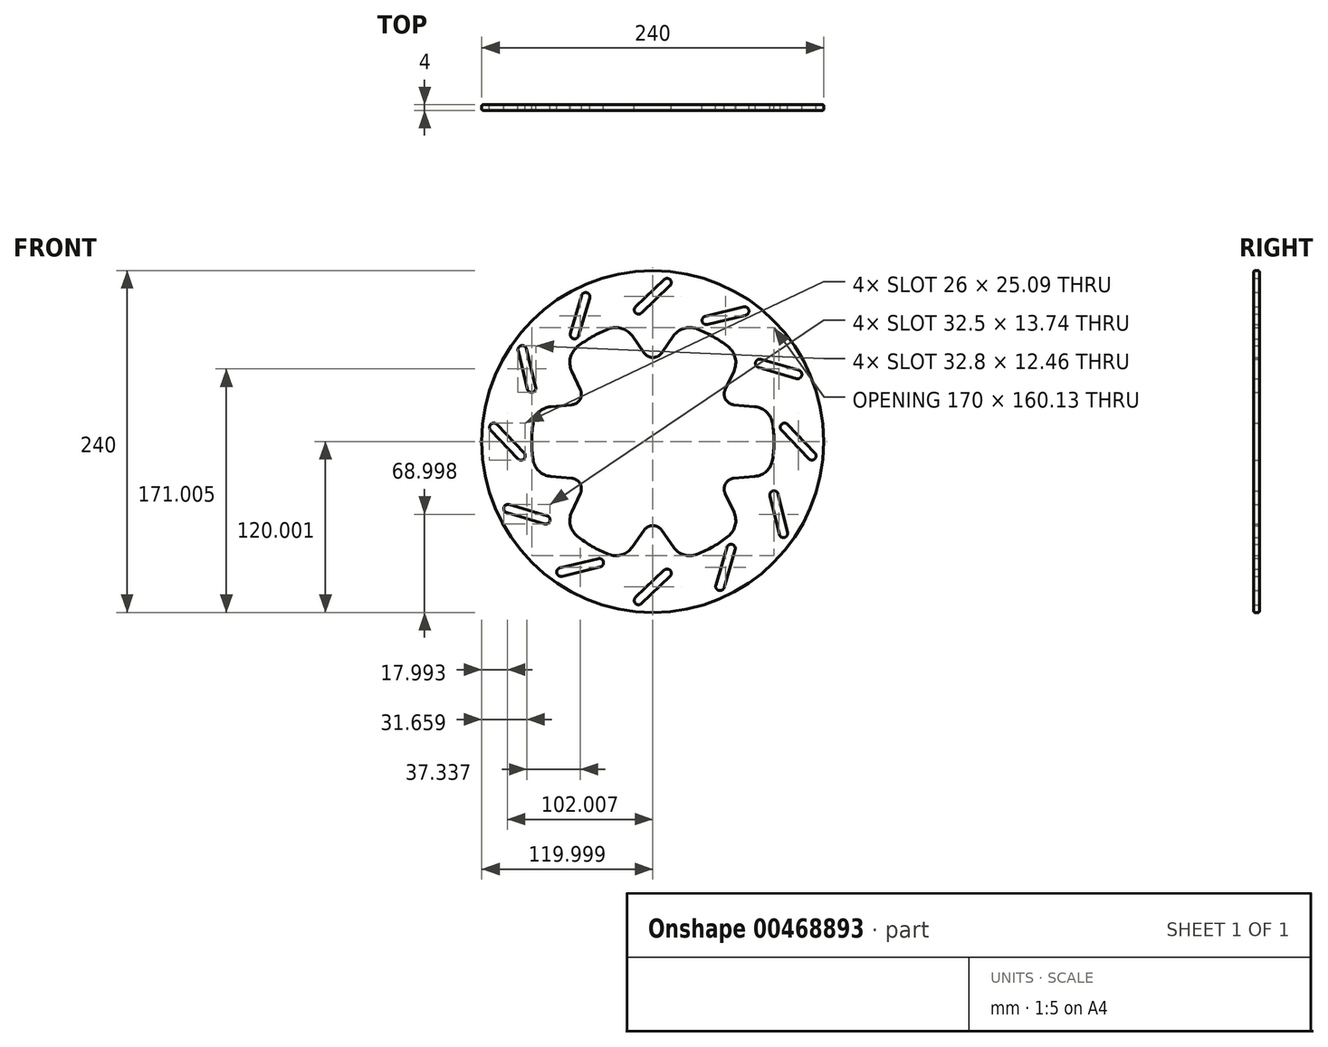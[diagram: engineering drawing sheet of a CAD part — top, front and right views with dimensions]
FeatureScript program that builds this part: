
annotation { "Feature Type Name" : "Feature", "Feature Type Description" : "" }
export const myFeature = defineFeature(function(context is Context, id is Id, definition is map)
    precondition{}
    {
        {
            var Q0;
            Q0=qCreatedBy(makeId("Front.planeOp"),FACE);
            var sketch = newSketch(context, id + "F0", { "sketchPlane" : qUnion([Q0])});
            skLineSegment(sketch, "E0", {"start": v(7.32, 64.91) * mm, "end": v(7.52, 65.27) * mm});
            skCircle(sketch, "E1", {"center": v(0.77, 5.27) * mm, "radius": 120 * mm});
            skArc(sketch, "E2", {"start": v(31.87, 84.38) * mm, "mid": v(22.72, 84.76) * mm, "end": v(15.3, 79.4) * mm});
            skLineSegment(sketch, "E3", {"start": v(15.3, 79.4) * mm, "end": v(6.9, 67.46) * mm});
            skArc(sketch, "E4", {"start": v(0.77, 64.27) * mm, "mid": v(4.23, 65.12) * mm, "end": v(6.9, 67.46) * mm});
            skArc(sketch, "E5", {"start": v(-13.76, 79.4) * mm, "mid": v(-21.18, 84.76) * mm, "end": v(-30.33, 84.38) * mm});
            skLineSegment(sketch, "E6", {"start": v(-13.76, 79.4) * mm, "end": v(-5.37, 67.46) * mm});
            skArc(sketch, "E7", {"start": v(-5.37, 67.46) * mm, "mid": v(-2.69, 65.12) * mm, "end": v(0.77, 64.27) * mm});
            skArc(sketch, "E8", {"start": v(-52.19, 71.76) * mm, "mid": v(-57.09, 64.03) * mm, "end": v(-56.16, 54.91) * mm});
            skLineSegment(sketch, "E9", {"start": v(-56.16, 54.91) * mm, "end": v(-50.02, 41.68) * mm});
            skLineSegment(sketch, "E10", {"start": v(-47.6, 40.76) * mm, "end": v(-47.82, 41.12) * mm});
            skArc(sketch, "E11", {"start": v(-56.15, 31.05) * mm, "mid": v(-52.79, 32.2) * mm, "end": v(-50.33, 34.77) * mm});
            skArc(sketch, "E12", {"start": v(-50.33, 34.77) * mm, "mid": v(-49.33, 38.19) * mm, "end": v(-50.02, 41.68) * mm});
            skLineSegment(sketch, "E13", {"start": v(-70.69, 29.75) * mm, "end": v(-56.15, 31.05) * mm});
            skArc(sketch, "E14", {"start": v(-70.69, 29.75) * mm, "mid": v(-79.04, 26) * mm, "end": v(-83.29, 17.89) * mm});
            skArc(sketch, "E15", {"start": v(-83.29, -7.34) * mm, "mid": v(-79.04, -15.46) * mm, "end": v(-70.69, -19.21) * mm});
            skLineSegment(sketch, "E16", {"start": v(-70.69, -19.21) * mm, "end": v(-56.15, -20.5) * mm});
            skLineSegment(sketch, "E17", {"start": v(-54.16, -18.88) * mm, "end": v(-54.57, -18.88) * mm});
            skArc(sketch, "E18", {"start": v(-50.02, -31.14) * mm, "mid": v(-49.33, -27.65) * mm, "end": v(-50.33, -24.23) * mm});
            skArc(sketch, "E19", {"start": v(-50.33, -24.23) * mm, "mid": v(-52.79, -21.66) * mm, "end": v(-56.15, -20.5) * mm});
            skLineSegment(sketch, "E20", {"start": v(-56.16, -44.37) * mm, "end": v(-50.02, -31.14) * mm});
            skArc(sketch, "E21", {"start": v(-56.16, -44.37) * mm, "mid": v(-57.09, -53.48) * mm, "end": v(-52.19, -61.22) * mm});
            skArc(sketch, "E22", {"start": v(-30.33, -73.83) * mm, "mid": v(-21.18, -74.21) * mm, "end": v(-13.76, -68.85) * mm});
            skLineSegment(sketch, "E23", {"start": v(-13.76, -68.85) * mm, "end": v(-5.37, -56.92) * mm});
            skLineSegment(sketch, "E24", {"start": v(-5.78, -54.37) * mm, "end": v(-5.98, -54.73) * mm});
            skArc(sketch, "E25", {"start": v(6.9, -56.92) * mm, "mid": v(4.23, -54.57) * mm, "end": v(0.77, -53.73) * mm});
            skArc(sketch, "E26", {"start": v(0.77, -53.73) * mm, "mid": v(-2.69, -54.57) * mm, "end": v(-5.37, -56.92) * mm});
            skLineSegment(sketch, "E27", {"start": v(15.3, -68.85) * mm, "end": v(6.9, -56.92) * mm});
            skArc(sketch, "E28", {"start": v(15.3, -68.85) * mm, "mid": v(22.72, -74.21) * mm, "end": v(31.87, -73.83) * mm});
            skArc(sketch, "E29", {"start": v(53.72, -61.22) * mm, "mid": v(58.63, -53.48) * mm, "end": v(57.7, -44.37) * mm});
            skLineSegment(sketch, "E30", {"start": v(57.7, -44.37) * mm, "end": v(51.56, -31.14) * mm});
            skLineSegment(sketch, "E31", {"start": v(49.15, -30.22) * mm, "end": v(49.36, -30.57) * mm});
            skArc(sketch, "E32", {"start": v(57.7, -20.5) * mm, "mid": v(54.32, -21.66) * mm, "end": v(51.86, -24.23) * mm});
            skArc(sketch, "E33", {"start": v(51.86, -24.23) * mm, "mid": v(50.87, -27.65) * mm, "end": v(51.56, -31.14) * mm});
            skLineSegment(sketch, "E34", {"start": v(72.23, -19.21) * mm, "end": v(57.7, -20.5) * mm});
            skArc(sketch, "E35", {"start": v(72.23, -19.21) * mm, "mid": v(80.58, -15.46) * mm, "end": v(84.83, -7.34) * mm});
            skArc(sketch, "E36", {"start": v(84.83, 17.89) * mm, "mid": v(80.58, 26) * mm, "end": v(72.23, 29.75) * mm});
            skLineSegment(sketch, "E37", {"start": v(72.23, 29.75) * mm, "end": v(57.7, 31.05) * mm});
            skLineSegment(sketch, "E38", {"start": v(55.7, 29.42) * mm, "end": v(56.1, 29.43) * mm});
            skArc(sketch, "E39", {"start": v(51.56, 41.68) * mm, "mid": v(50.87, 38.19) * mm, "end": v(51.86, 34.77) * mm});
            skArc(sketch, "E40", {"start": v(51.86, 34.77) * mm, "mid": v(54.32, 32.2) * mm, "end": v(57.7, 31.05) * mm});
            skLineSegment(sketch, "E41", {"start": v(57.7, 54.91) * mm, "end": v(51.56, 41.68) * mm});
            skArc(sketch, "E42", {"start": v(57.7, 54.91) * mm, "mid": v(58.63, 64.03) * mm, "end": v(53.72, 71.76) * mm});
            skArc(sketch, "E43", {"start": v(53.72, 71.76) * mm, "mid": v(43.27, 78.88) * mm, "end": v(31.87, 84.38) * mm});
            skArc(sketch, "E44", {"start": v(-30.33, 84.38) * mm, "mid": v(-41.73, 78.88) * mm, "end": v(-52.19, 71.76) * mm});
            skArc(sketch, "E45", {"start": v(-83.29, 17.89) * mm, "mid": v(-84.23, 5.27) * mm, "end": v(-83.29, -7.34) * mm});
            skArc(sketch, "E46", {"start": v(-52.19, -61.22) * mm, "mid": v(-41.73, -68.34) * mm, "end": v(-30.33, -73.83) * mm});
            skArc(sketch, "E47", {"start": v(31.87, -73.83) * mm, "mid": v(43.27, -68.34) * mm, "end": v(53.72, -61.22) * mm});
            skArc(sketch, "E48", {"start": v(84.83, -7.34) * mm, "mid": v(85.77, 5.27) * mm, "end": v(84.83, 17.89) * mm});
            skLineSegment(sketch, "E49", {"start": v(-108.61, 17.34) * mm, "end": v(-89.52, -2.66) * mm});
            skLineSegment(sketch, "E50", {"start": v(-112.95, 13.2) * mm, "end": v(-93.86, -6.8) * mm});
            skArc(sketch, "E51", {"start": v(-108.61, 17.34) * mm, "mid": v(-112.85, 17.44) * mm, "end": v(-112.95, 13.2) * mm});
            skArc(sketch, "E52", {"start": v(-93.86, -6.8) * mm, "mid": v(-89.62, -6.9) * mm, "end": v(-89.52, -2.66) * mm});
            skArc(sketch, "E53", {"start": v(-100, -38.97) * mm, "mid": v(-103.72, -41) * mm, "end": v(-101.68, -44.72) * mm});
            skLineSegment(sketch, "E54", {"start": v(-100, -38.97) * mm, "end": v(-73.46, -46.74) * mm});
            skLineSegment(sketch, "E55", {"start": v(-101.68, -44.72) * mm, "end": v(-75.15, -52.5) * mm});
            skArc(sketch, "E56", {"start": v(-75.15, -52.5) * mm, "mid": v(-71.43, -50.46) * mm, "end": v(-73.46, -46.74) * mm});
            skArc(sketch, "E57", {"start": v(-64.38, -83.42) * mm, "mid": v(-66.58, -87.05) * mm, "end": v(-62.96, -89.25) * mm});
            skLineSegment(sketch, "E58", {"start": v(-64.38, -83.42) * mm, "end": v(-37.5, -76.89) * mm});
            skLineSegment(sketch, "E59", {"start": v(-62.96, -89.25) * mm, "end": v(-36.1, -82.72) * mm});
            skArc(sketch, "E60", {"start": v(-36.1, -82.72) * mm, "mid": v(-33.89, -79.1) * mm, "end": v(-37.5, -76.89) * mm});
            skArc(sketch, "E61", {"start": v(-11.3, -104.11) * mm, "mid": v(-11.4, -108.35) * mm, "end": v(-7.16, -108.45) * mm});
            skLineSegment(sketch, "E62", {"start": v(-11.3, -104.11) * mm, "end": v(8.7, -85.02) * mm});
            skLineSegment(sketch, "E63", {"start": v(-7.16, -108.45) * mm, "end": v(12.84, -89.36) * mm});
            skArc(sketch, "E64", {"start": v(12.84, -89.36) * mm, "mid": v(12.94, -85.12) * mm, "end": v(8.7, -85.02) * mm});
            skArc(sketch, "E65", {"start": v(45, -95.5) * mm, "mid": v(47.04, -99.22) * mm, "end": v(50.76, -97.18) * mm});
            skLineSegment(sketch, "E66", {"start": v(45, -95.5) * mm, "end": v(52.78, -68.96) * mm});
            skLineSegment(sketch, "E67", {"start": v(50.76, -97.18) * mm, "end": v(58.54, -70.65) * mm});
            skArc(sketch, "E68", {"start": v(58.54, -70.65) * mm, "mid": v(56.5, -66.92) * mm, "end": v(52.78, -68.96) * mm});
            skArc(sketch, "E69", {"start": v(89.46, -59.87) * mm, "mid": v(93.09, -62.08) * mm, "end": v(95.3, -58.46) * mm});
            skLineSegment(sketch, "E70", {"start": v(89.46, -59.87) * mm, "end": v(82.93, -33) * mm});
            skLineSegment(sketch, "E71", {"start": v(95.3, -58.46) * mm, "end": v(88.76, -31.6) * mm});
            skArc(sketch, "E72", {"start": v(88.76, -31.6) * mm, "mid": v(85.13, -29.38) * mm, "end": v(82.93, -33) * mm});
            skArc(sketch, "E73", {"start": v(110.15, -6.8) * mm, "mid": v(114.4, -6.9) * mm, "end": v(114.5, -2.66) * mm});
            skLineSegment(sketch, "E74", {"start": v(110.15, -6.8) * mm, "end": v(91.06, 13.2) * mm});
            skLineSegment(sketch, "E75", {"start": v(114.5, -2.66) * mm, "end": v(95.4, 17.34) * mm});
            skArc(sketch, "E76", {"start": v(95.4, 17.34) * mm, "mid": v(91.16, 17.44) * mm, "end": v(91.06, 13.2) * mm});
            skArc(sketch, "E77", {"start": v(101.53, 49.5) * mm, "mid": v(105.26, 51.54) * mm, "end": v(103.22, 55.27) * mm});
            skLineSegment(sketch, "E78", {"start": v(101.53, 49.5) * mm, "end": v(75, 57.28) * mm});
            skLineSegment(sketch, "E79", {"start": v(103.22, 55.27) * mm, "end": v(76.69, 63.04) * mm});
            skArc(sketch, "E80", {"start": v(76.69, 63.04) * mm, "mid": v(72.96, 61) * mm, "end": v(75, 57.28) * mm});
            skArc(sketch, "E81", {"start": v(65.91, 93.96) * mm, "mid": v(68.12, 97.59) * mm, "end": v(64.5, 99.8) * mm});
            skLineSegment(sketch, "E82", {"start": v(65.91, 93.96) * mm, "end": v(39.05, 87.43) * mm});
            skLineSegment(sketch, "E83", {"start": v(64.5, 99.8) * mm, "end": v(37.63, 93.26) * mm});
            skArc(sketch, "E84", {"start": v(37.63, 93.26) * mm, "mid": v(35.42, 89.64) * mm, "end": v(39.05, 87.43) * mm});
            skArc(sketch, "E85", {"start": v(12.84, 114.65) * mm, "mid": v(12.94, 118.9) * mm, "end": v(8.7, 119) * mm});
            skLineSegment(sketch, "E86", {"start": v(12.84, 114.65) * mm, "end": v(-7.16, 95.56) * mm});
            skLineSegment(sketch, "E87", {"start": v(8.7, 119) * mm, "end": v(-11.3, 99.9) * mm});
            skArc(sketch, "E88", {"start": v(-11.3, 99.9) * mm, "mid": v(-11.4, 95.66) * mm, "end": v(-7.16, 95.56) * mm});
            skArc(sketch, "E89", {"start": v(-43.47, 106.04) * mm, "mid": v(-45.5, 109.76) * mm, "end": v(-49.23, 107.72) * mm});
            skLineSegment(sketch, "E90", {"start": v(-43.47, 106.04) * mm, "end": v(-51.24, 79.5) * mm});
            skLineSegment(sketch, "E91", {"start": v(-49.23, 107.72) * mm, "end": v(-57, 81.19) * mm});
            skArc(sketch, "E92", {"start": v(-57, 81.19) * mm, "mid": v(-54.96, 77.47) * mm, "end": v(-51.24, 79.5) * mm});
            skArc(sketch, "E93", {"start": v(-87.92, 70.42) * mm, "mid": v(-91.55, 72.62) * mm, "end": v(-93.75, 69) * mm});
            skLineSegment(sketch, "E94", {"start": v(-87.92, 70.42) * mm, "end": v(-81.39, 43.55) * mm});
            skLineSegment(sketch, "E95", {"start": v(-93.75, 69) * mm, "end": v(-87.22, 42.13) * mm});
            skArc(sketch, "E96", {"start": v(-87.22, 42.13) * mm, "mid": v(-83.6, 39.93) * mm, "end": v(-81.39, 43.55) * mm});
            skSolve(sketch);
        }
        {
            var Q0;
            Q0 = qSketchRegion(id + "F0", true);
            extrude(context, id + "F1", {"entities" : qUnion([Q0]), "depth" : 4 * mm});
        }
        {
            var Q0;
            Q0=makeQuery(id+"F1.opExtrude","CAP_EDGE",EDGE,{"disambiguationData":[OSD([sQuery(id+"F0.wireOp",EDGE,"E1")])],"isStart":false});
            fillet(context, id + "F2", {"entities" : qUnion([Q0]), "radius" : 1 * mm, "tangentPropagation" : true, "allowEdgeOverflow" : false});
        }
        {
            var Q0;
            Q0=makeQuery(id+"F1.opExtrude","CAP_EDGE",EDGE,{"disambiguationData":[OSD([sQuery(id+"F0.wireOp",EDGE,"E1")])],"isStart":true});
            fillet(context, id + "F3", {"entities" : qUnion([Q0]), "radius" : 1 * mm, "tangentPropagation" : true, "allowEdgeOverflow" : false});
        }
    });
